# Revit family: Гольфстрим_Радиусный_R
name_source: partatom
category: Оборудование
units: mm (PartAtom-declared; Revit-internal decimal feet)

## family parameters
Всегда вертикально = Да
Классификация = Нет
На основе рабочей плоскости = Нет
Общий = Нет
При загрузке вырезать с полостями = Нет
Размер круглого соединителя = Использовать диаметр
Тип детали = Нормальный
Точка расчета площади = Нет

## types (1)
- Стандарт
    ADSK_Размер_Высота = 80 мм
    ADSK_Размер_Длина = 5000 мм
    ADSK_Размер_Ширина = 200 мм
    Qну_dT50 = 0 Вт
    Qну_dT60 = 0 Вт
    Qну_dT70 = 0 Вт
    U = -70 мм
    n = 255
    r1 = 4525 мм
    r2 = 4475 мм
    Материал кронштейна = Окраска - RAL 9016, белый дорожный
    Материал панели = Окраска - RAL 9016, белый дорожный
    Материал решетки = Окраска - RAL 7021, черно-серый
    Межосевое расстояние = 50 мм
    Номинальный диаметр = 15 мм
    Отступ от пола = 100 мм
    Радиус = 8 мм
    Радиус конвектора = 4500 мм
    Толщина стенки панели = 7 мм
    Угол = 63.66°
    Ширина решетки = 186 мм

## geometry (parser evidence)
native form markers: Blend x2
no freeform markers — native parametric forms only
